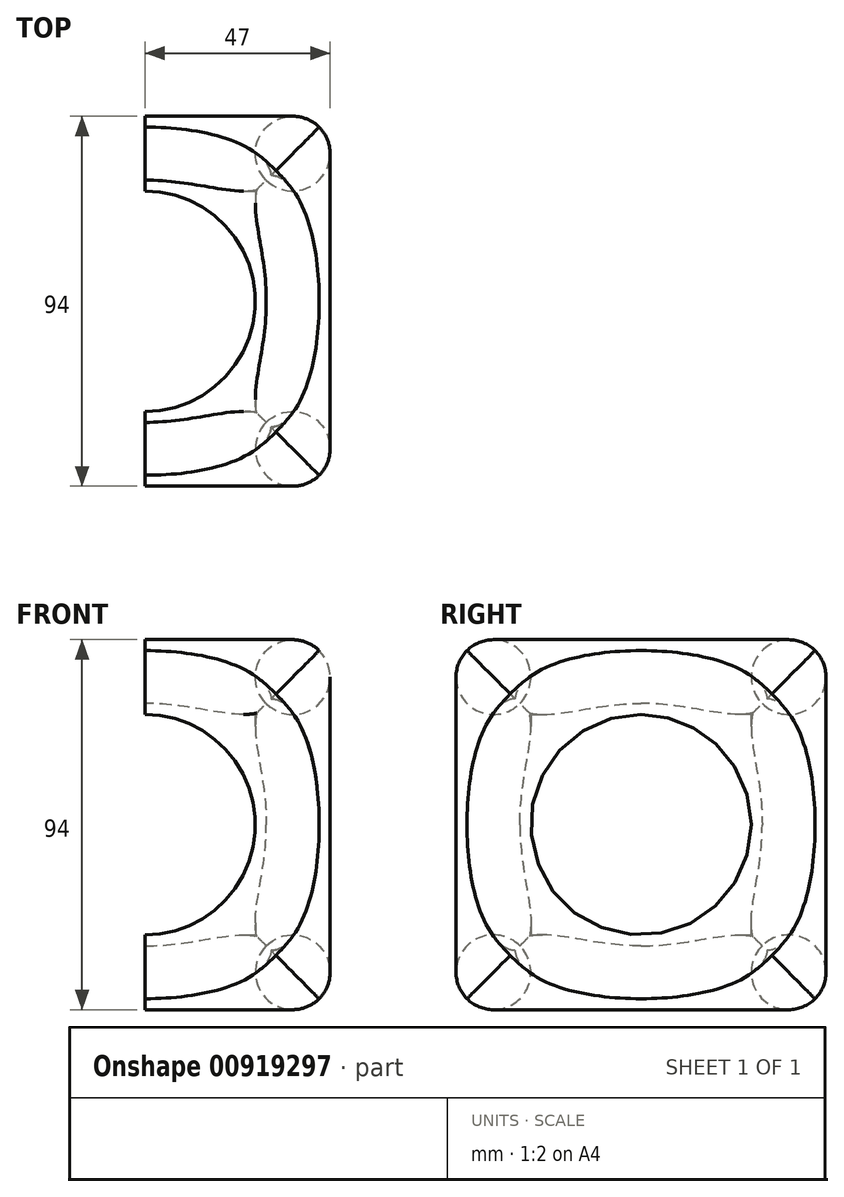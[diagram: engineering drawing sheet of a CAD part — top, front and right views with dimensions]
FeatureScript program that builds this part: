
annotation { "Feature Type Name" : "Feature", "Feature Type Description" : "" }
export const myFeature = defineFeature(function(context is Context, id is Id, definition is map)
    precondition{}
    {
        {
            var Q0;
            Q0=qCreatedBy(makeId("Top.planeOp"),FACE);
            var sketch = newSketch(context, id + "F0", { "sketchPlane" : qUnion([Q0])});
            skCircle(sketch, "E0", {"center": v(0, 0) * mm, "radius": 32 * mm});
            skCircle(sketch, "E1", {"center": v(0, 0) * mm, "radius": 53.03 * mm, "construction": true});
            skLineSegment(sketch, "E2.bottom", {"start": v(43, 43) * mm, "end": v(-43, 43) * mm, "construction": true});
            skLineSegment(sketch, "E2.top", {"start": v(43, -43) * mm, "end": v(-43, -43) * mm, "construction": true});
            skLineSegment(sketch, "E2.left", {"start": v(43, 43) * mm, "end": v(43, -43) * mm, "construction": true});
            skLineSegment(sketch, "E2.right", {"start": v(-43, 43) * mm, "end": v(-43, -43) * mm, "construction": true});
            skCircle(sketch, "E3", {"center": v(-37.5, 37.5) * mm, "radius": 5.5 * mm, "construction": true});
            skCircle(sketch, "E4", {"center": v(-37.5, -37.5) * mm, "radius": 5.5 * mm, "construction": true});
            skCircle(sketch, "E5", {"center": v(37.5, -37.5) * mm, "radius": 5.5 * mm, "construction": true});
            skCircle(sketch, "E6", {"center": v(37.5, 37.5) * mm, "radius": 5.5 * mm, "construction": true});
            skLineSegment(sketch, "E7", {"start": v(37.5, 37.5) * mm, "end": v(-37.5, 37.5) * mm, "construction": true});
            skLineSegment(sketch, "E8", {"start": v(-37.5, 37.5) * mm, "end": v(-37.5, -37.5) * mm, "construction": true});
            skLineSegment(sketch, "E9", {"start": v(37.5, -37.5) * mm, "end": v(-37.5, -37.5) * mm, "construction": true});
            skLineSegment(sketch, "E10", {"start": v(37.5, -37.5) * mm, "end": v(37.5, 37.5) * mm, "construction": true});
            skPoint(sketch, "E11.endSnap0", {"position": v(37.5, 0) * mm});
            skCircle(sketch, "E12", {"center": v(-37.5, -37.5) * mm, "radius": 9.5 * mm});
            skCircle(sketch, "E13", {"center": v(-37.5, 37.5) * mm, "radius": 9.5 * mm});
            skCircle(sketch, "E14", {"center": v(37.5, 37.5) * mm, "radius": 9.5 * mm});
            skCircle(sketch, "E15", {"center": v(37.5, -37.5) * mm, "radius": 9.5 * mm});
            skLineSegment(sketch, "E16", {"start": v(0, 0) * mm, "end": v(20.97, 0) * mm, "construction": true});
            skLineSegment(sketch, "E17", {"start": v(0, 0) * mm, "end": v(0, -17.54) * mm, "construction": true});
            skSolve(sketch);
        }
        {
            var Q0;
            Q0=qCreatedBy(makeId("Right.planeOp"),FACE);
            var sketch = newSketch(context, id + "F1", { "sketchPlane" : qUnion([Q0])});
            skCircle(sketch, "E18", {"center": v(0, 0) * mm, "radius": 32 * mm});
            skCircle(sketch, "E19", {"center": v(0, 0) * mm, "radius": 53.03 * mm, "construction": true});
            skCircle(sketch, "E20", {"center": v(-37.5, 37.5) * mm, "radius": 5.5 * mm, "construction": true});
            skCircle(sketch, "E21", {"center": v(-37.5, -37.5) * mm, "radius": 5.5 * mm, "construction": true});
            skCircle(sketch, "E22", {"center": v(37.5, -37.5) * mm, "radius": 5.5 * mm, "construction": true});
            skCircle(sketch, "E23", {"center": v(37.5, 37.5) * mm, "radius": 5.5 * mm, "construction": true});
            skLineSegment(sketch, "E24", {"start": v(37.5, 37.5) * mm, "end": v(-37.5, 37.5) * mm, "construction": true});
            skLineSegment(sketch, "E25", {"start": v(-37.5, 37.5) * mm, "end": v(-37.5, -37.5) * mm, "construction": true});
            skLineSegment(sketch, "E26", {"start": v(37.5, -37.5) * mm, "end": v(-37.5, -37.5) * mm, "construction": true});
            skLineSegment(sketch, "E27", {"start": v(37.5, -37.5) * mm, "end": v(37.5, 37.5) * mm, "construction": true});
            skPoint(sketch, "E28.endSnap0", {"position": v(37.5, 0) * mm});
            skCircle(sketch, "E29", {"center": v(-37.5, -37.5) * mm, "radius": 9.5 * mm});
            skCircle(sketch, "E30", {"center": v(37.5, -37.5) * mm, "radius": 9.5 * mm});
            skLineSegment(sketch, "E31", {"start": v(0, 0) * mm, "end": v(0, 65.95) * mm, "construction": true});
            skCircle(sketch, "E32", {"center": v(-37.5, 37.5) * mm, "radius": 9.5 * mm});
            skLineSegment(sketch, "E33", {"start": v(0, 0) * mm, "end": v(28.28, 0) * mm, "construction": true});
            skSolve(sketch);
        }
        {
            var Q0;
            Q0=makeQuery(id+"F1.imprint","IMPRINT",FACE,{"disambiguationData":[TD([[makeQuery(id+"F1.imprint","IMPRINT",EDGE,{"derivedFrom":sQuery(id+"F1.wireOp",EDGE,"E29")}),1.0]])]});
            var Q1;
            Q1=makeQuery(id+"F1.imprint","IMPRINT",FACE,{"disambiguationData":[TD([[makeQuery(id+"F1.imprint","IMPRINT",EDGE,{"derivedFrom":sQuery(id+"F1.wireOp",EDGE,"E32")}),1.0]])]});
            var Q2;
            Q2=sQuery(id+"F1.wireOp",EDGE,"E29");
            var Q3;
            Q3=sQuery(id+"F1.wireOp",EDGE,"E31");
            revolve(context, id + "F2", {"surfaceOperationType" : NewSurfaceOperationType.NEW, "entities" : qUnion([Q0, Q1]), "surfaceEntities" : qUnion([Q2]), "axis" : qUnion([Q3]), "revolveType" : RevolveType.FULL});
        }
        {
            var Q0;
            Q0=makeQuery(id+"F1.imprint","IMPRINT",FACE,{"disambiguationData":[TD([[makeQuery(id+"F1.imprint","IMPRINT",EDGE,{"derivedFrom":sQuery(id+"F1.wireOp",EDGE,"E32")}),1.0]])]});
            var Q1;
            Q1=makeQuery(id+"F1.imprint","IMPRINT",FACE,{"disambiguationData":[TD([[makeQuery(id+"F1.imprint","IMPRINT",EDGE,{"derivedFrom":sQuery(id+"F1.wireOp",EDGE,"E30")}),1.0]])]});
            var Q2;
            Q2=sQuery(id+"F1.wireOp",EDGE,"E33");
            revolve(context, id + "F3", {"operationType" : NewBodyOperationType.ADD, "surfaceOperationType" : NewSurfaceOperationType.NEW, "entities" : qUnion([Q0, Q1]), "axis" : qUnion([Q2]), "revolveType" : RevolveType.FULL});
        }
        {
            var Q0;
            Q0=makeQuery(id+"F0.imprint","IMPRINT",FACE,{"disambiguationData":[TD([[makeQuery(id+"F0.imprint","IMPRINT",EDGE,{"derivedFrom":sQuery(id+"F0.wireOp",EDGE,"E15")}),1.0]])]});
            var Q1;
            Q1=makeQuery(id+"F0.imprint","IMPRINT",FACE,{"disambiguationData":[TD([[makeQuery(id+"F0.imprint","IMPRINT",EDGE,{"derivedFrom":sQuery(id+"F0.wireOp",EDGE,"E12")}),1.0]])]});
            var Q2;
            Q2=sQuery(id+"F0.wireOp",EDGE,"E16");
            revolve(context, id + "F4", {"operationType" : NewBodyOperationType.ADD, "surfaceOperationType" : NewSurfaceOperationType.NEW, "entities" : qUnion([Q0, Q1]), "axis" : qUnion([Q2]), "revolveType" : RevolveType.FULL});
        }
        {
            var Q0;
            Q0=qCreatedBy(makeId("Right.planeOp"),FACE);
            var sketch = newSketch(context, id + "F5", { "sketchPlane" : qUnion([Q0])});
            skLineSegment(sketch, "E34.bottom", {"start": v(-61.15, -48.38) * mm, "end": v(72.64, -48.38) * mm});
            skLineSegment(sketch, "E34.top", {"start": v(-61.15, 57.51) * mm, "end": v(72.64, 57.51) * mm});
            skLineSegment(sketch, "E34.left", {"start": v(-61.15, -48.38) * mm, "end": v(-61.15, 57.51) * mm});
            skLineSegment(sketch, "E34.right", {"start": v(72.64, -48.38) * mm, "end": v(72.64, 57.51) * mm});
            skSolve(sketch);
        }
        {
            var Q0;
            Q0=makeQuery(id+"F5.imprint","IMPRINT",FACE,{"disambiguationData":[TD([[makeQuery(id+"F5.imprint","IMPRINT",EDGE,{"derivedFrom":sQuery(id+"F5.wireOp",EDGE,"E34.bottom")}),1.0]])]});
            extrude(context, id + "F6", {"entities" : qUnion([Q0]), "operationType" : NewBodyOperationType.REMOVE, "oppositeDirection" : true, "depth" : 84.8 * mm, "offsetDistance" : 25 * mm});
        }
    });
